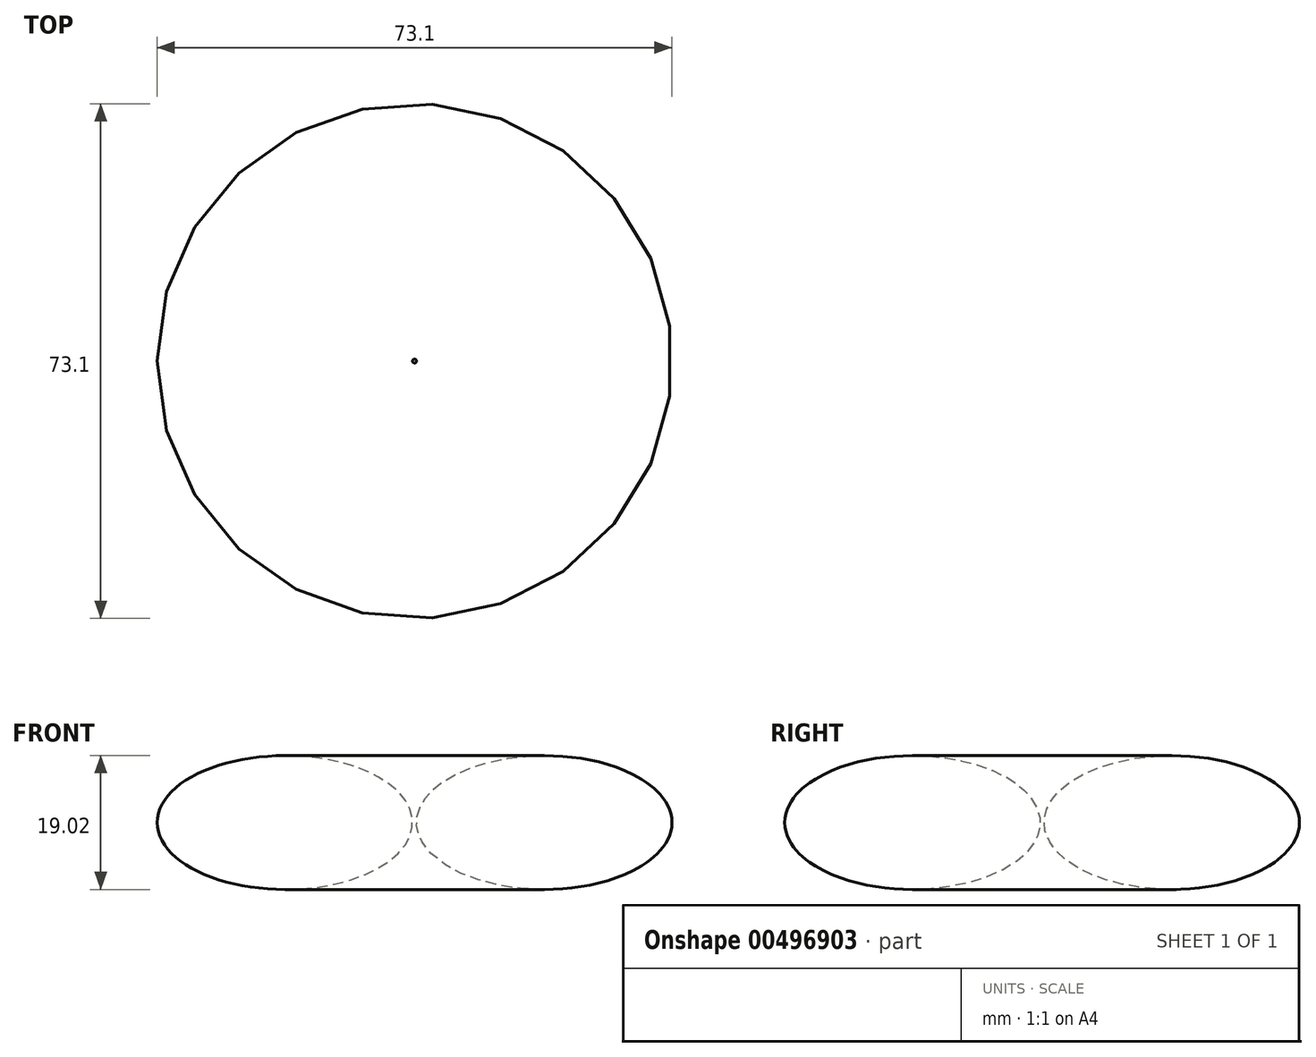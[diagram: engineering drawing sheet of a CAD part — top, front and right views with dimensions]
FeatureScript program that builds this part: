
annotation { "Feature Type Name" : "Feature", "Feature Type Description" : "" }
export const myFeature = defineFeature(function(context is Context, id is Id, definition is map)
    precondition{}
    {
        {
            var Q0;
            Q0=qCreatedBy(makeId("Front.planeOp"),FACE);
            var sketch = newSketch(context, id + "F0", { "sketchPlane" : qUnion([Q0])});
            skEllipse(sketch, "E0", {"center": v(-18.42, 0) * mm, "majorRadius": 18.13 * mm, "minorRadius": 9.5 * mm, "majorAxis": v(-1, 0)});
            skSolve(sketch);
        }
        {
            var Q0;
            Q0=qCreatedBy(makeId("Front.planeOp"),FACE);
            var sketch = newSketch(context, id + "F1", { "sketchPlane" : qUnion([Q0])});
            skLineSegment(sketch, "E1", {"start": v(0, 11.8) * mm, "end": v(0, -8.35) * mm});
            skSolve(sketch);
        }
        {
            var Q0;
            Q0=makeQuery(id+"F0.imprint","IMPRINT",FACE,{"disambiguationData":[TD([[makeQuery(id+"F0.imprint","IMPRINT",EDGE,{"derivedFrom":sQuery(id+"F0.wireOp",EDGE,"E0")}),1.0]])]});
            var Q1;
            Q1=sQuery(id+"F1.wireOp",EDGE,"E1");
            revolve(context, id + "F2", {"entities" : qUnion([Q0]), "axis" : qUnion([Q1]), "revolveType" : RevolveType.FULL});
        }
    });
